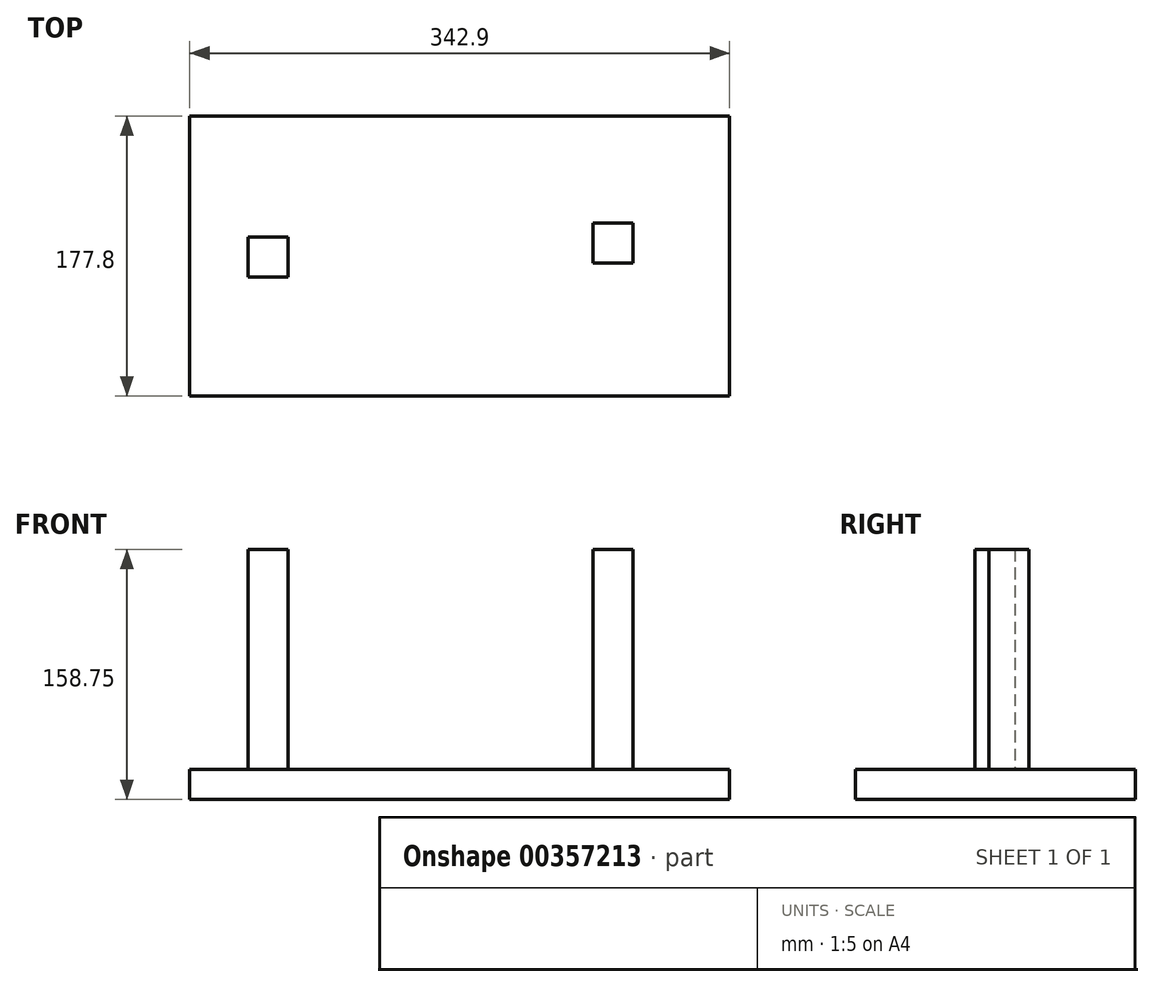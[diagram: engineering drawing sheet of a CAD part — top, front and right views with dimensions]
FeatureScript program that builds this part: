
annotation { "Feature Type Name" : "Feature", "Feature Type Description" : "" }
export const myFeature = defineFeature(function(context is Context, id is Id, definition is map)
    precondition{}
    {
        {
            var Q0;
            Q0=qCreatedBy(makeId("Top.planeOp"),FACE);
            var sketch = newSketch(context, id + "F0", { "sketchPlane" : qUnion([Q0])});
            skLineSegment(sketch, "E0.bottom", {"start": v(-173.27, 111.05) * mm, "end": v(169.63, 111.05) * mm});
            skLineSegment(sketch, "E0.top", {"start": v(-173.27, -66.75) * mm, "end": v(169.63, -66.75) * mm});
            skLineSegment(sketch, "E0.left", {"start": v(-173.27, 111.05) * mm, "end": v(-173.27, -66.75) * mm});
            skLineSegment(sketch, "E0.right", {"start": v(169.63, 111.05) * mm, "end": v(169.63, -66.75) * mm});
            skSolve(sketch);
        }
        {
            var Q0;
            Q0 = qSketchRegion(id + "F0", true);
            extrude(context, id + "F1", {"entities" : qUnion([Q0]), "depth" : 19.05 * mm});
        }
        {
            var Q0;
            Q0=makeQuery(id+"F1.opExtrude","CAP_FACE",FACE,{"disambiguationData":[OSD([sQuery(id+"F0.wireOp",EDGE,"E0.bottom"),sQuery(id+"F0.wireOp",EDGE,"E0.top"),sQuery(id+"F0.wireOp",EDGE,"E0.left"),sQuery(id+"F0.wireOp",EDGE,"E0.right")])],"isStart":false});
            var sketch = newSketch(context, id + "F2", { "sketchPlane" : qUnion([Q0])});
            skLineSegment(sketch, "E1.bottom", {"start": v(82.8, 43.24) * mm, "end": v(108.2, 43.24) * mm});
            skLineSegment(sketch, "E1.top", {"start": v(82.8, 17.84) * mm, "end": v(108.2, 17.84) * mm});
            skLineSegment(sketch, "E1.left", {"start": v(82.8, 43.24) * mm, "end": v(82.8, 17.84) * mm});
            skLineSegment(sketch, "E1.right", {"start": v(108.2, 43.24) * mm, "end": v(108.2, 17.84) * mm});
            skLineSegment(sketch, "E2.left", {"start": v(99.61, 47.7) * mm, "end": v(99.61, 47.36) * mm});
            skLineSegment(sketch, "E2.right", {"start": v(79.02, 47.7) * mm, "end": v(79.02, 47.36) * mm});
            skSolve(sketch);
        }
        {
            var Q0;
            Q0 = qSketchRegion(id + "F2", true);
            extrude(context, id + "F3", {"entities" : qUnion([Q0]), "operationType" : NewBodyOperationType.ADD, "depth" : 139.7 * mm});
        }
        {
            var Q0;
            Q0=makeQuery(id+"F1.opExtrude","CAP_FACE",FACE,{"disambiguationData":[OSD([sQuery(id+"F0.wireOp",EDGE,"E0.bottom"),sQuery(id+"F0.wireOp",EDGE,"E0.top"),sQuery(id+"F0.wireOp",EDGE,"E0.left"),sQuery(id+"F0.wireOp",EDGE,"E0.right")])],"isStart":false});
            var sketch = newSketch(context, id + "F4", { "sketchPlane" : qUnion([Q0])});
            skLineSegment(sketch, "E3.bottom", {"start": v(-136.38, 34.32) * mm, "end": v(-110.98, 34.32) * mm});
            skLineSegment(sketch, "E3.top", {"start": v(-136.38, 8.92) * mm, "end": v(-110.98, 8.92) * mm});
            skLineSegment(sketch, "E3.left", {"start": v(-136.38, 34.32) * mm, "end": v(-136.38, 8.92) * mm});
            skLineSegment(sketch, "E3.right", {"start": v(-110.98, 34.32) * mm, "end": v(-110.98, 8.92) * mm});
            skSolve(sketch);
        }
        {
            var Q0;
            Q0 = qSketchRegion(id + "F4", true);
            extrude(context, id + "F5", {"entities" : qUnion([Q0]), "operationType" : NewBodyOperationType.ADD, "depth" : 139.7 * mm});
        }
    });
